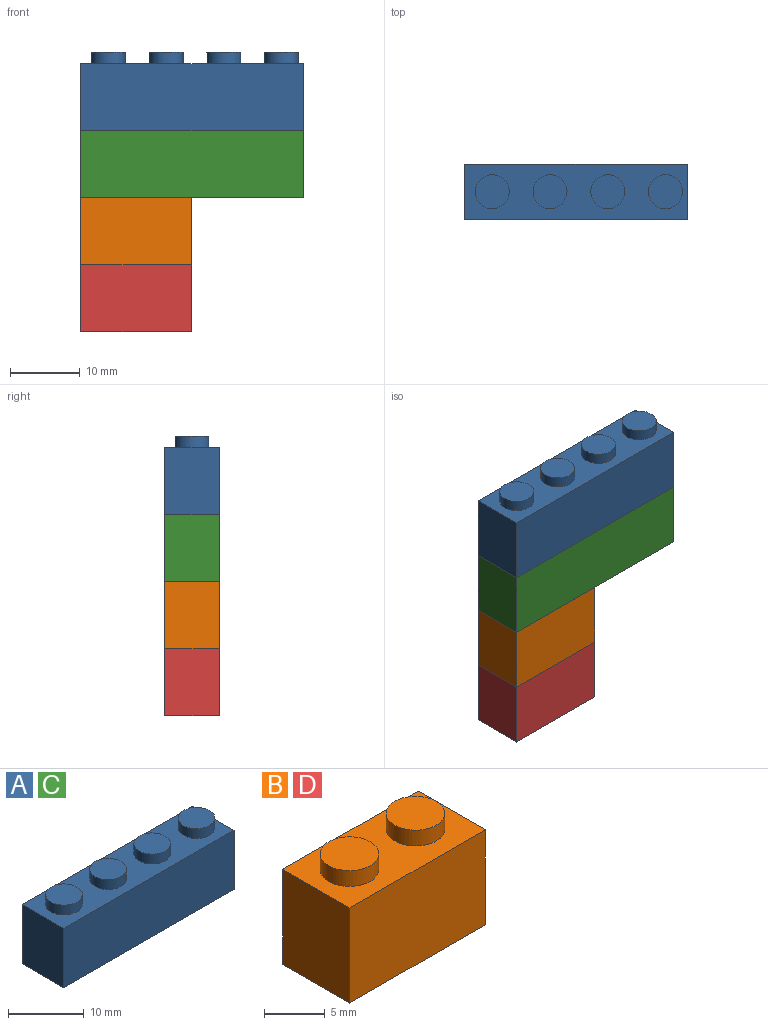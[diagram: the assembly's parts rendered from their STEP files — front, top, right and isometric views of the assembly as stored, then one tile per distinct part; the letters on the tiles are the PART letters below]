
ASSEMBLY  parts=4 mates=4
PART A: 25 faces, bbox 31.8x7.8x11.2 mm
  f0: plane 31.79x7.81mm, normal (0,0,-1), area 110.5mm2, adj f1,f2,f3,f4,f6,f7,f8,f12
  f1: plane 9.58x7.81mm, normal (1,0,0), area 74.8mm2, adj f0,f2,f4,f5
  f2: plane 31.79x9.58mm, normal (0,1,0), area 304.5mm2, adj f0,f1,f3,f5
  f3: plane 9.58x7.81mm, normal (-1,0,0), area 74.8mm2, adj f0,f2,f4,f5
  f4: plane 31.79x9.58mm, normal (0,-1,0), area 304.5mm2, adj f0,f1,f3,f5
  f5: plane 31.79x7.81mm, normal (0,0,1), area 174.1mm2, adj f1,f2,f3,f4,f17,f19,f21,f23
  f6: plane 28.77x8.05mm, normal (0,1,0), area 231.6mm2, adj f0,f7,f12,f13
  f7: plane 8.05x4.79mm, normal (1,0,0), area 38.6mm2, adj f0,f6,f8,f13
  f8: plane 28.77x8.05mm, normal (0,-1,0), area 231.6mm2, adj f0,f7,f12,f13
  f9: cylinder r=1.5mm len=8.05mm, axis (0,0,-1), area 75.6mm2, adj f13,f16
  f10: cylinder r=1.5mm len=8.05mm, axis (0,0,-1), area 75.6mm2, adj f13,f15
  f11: cylinder r=1.5mm len=8.05mm, axis (0,0,-1), area 75.6mm2, adj f13,f14
  f12: plane 8.05x4.79mm, normal (-1,0,0), area 38.6mm2, adj f0,f6,f8,f13
  f13: plane 28.77x4.79mm, normal (0,0,-1), area 116.7mm2, adj f6,f7,f8,f9,f10,f11,f12
  f14: plane 2.99x2.99mm, normal (0,0,-1), area 7mm2, adj f11
  f15: plane 2.99x2.99mm, normal (0,0,-1), area 7mm2, adj f10
  f16: plane 2.99x2.99mm, normal (0,0,-1), area 7mm2, adj f9
  f17: cylinder r=2.43mm len=4.86mm, axis (0,0,-1), area 24.3mm2, adj f5,f18
  f18: plane 4.86x4.86mm, normal (0,0,1), area 18.6mm2, adj f17
  f19: cylinder r=2.43mm len=4.86mm, axis (0,0,-1), area 24.3mm2, adj f5,f20
  f20: plane 4.86x4.86mm, normal (0,0,1), area 18.6mm2, adj f19
  f21: cylinder r=2.43mm len=4.86mm, axis (0,0,-1), area 24.3mm2, adj f5,f22
  f22: plane 4.86x4.86mm, normal (0,0,1), area 18.6mm2, adj f21
  f23: cylinder r=2.43mm len=4.86mm, axis (0,0,-1), area 24.3mm2, adj f5,f24
  f24: plane 4.86x4.86mm, normal (0,0,1), area 18.6mm2, adj f23
PART B: 17 faces, bbox 15.8x7.8x11.2 mm
  f0: plane 15.8x7.81mm, normal (0,0,-1), area 60.4mm2, adj f1,f2,f3,f4,f10,f11,f12,f13
  f1: plane 15.8x9.58mm, normal (0,1,0), area 151.4mm2, adj f0,f2,f4,f5
  f2: plane 9.58x7.81mm, normal (-1,0,0), area 74.8mm2, adj f0,f1,f3,f5
  f3: plane 15.8x9.58mm, normal (0,-1,0), area 151.4mm2, adj f0,f2,f4,f5
  f4: plane 9.58x7.81mm, normal (1,0,0), area 74.8mm2, adj f0,f1,f3,f5
  f5: plane 15.8x7.81mm, normal (0,0,1), area 86.8mm2, adj f1,f2,f3,f4,f6,f8
  f6: cylinder r=2.42mm len=4.83mm, axis (0,0,-1), area 24.1mm2, adj f5,f7
  f7: plane 4.83x4.83mm, normal (0,0,1), area 18.3mm2, adj f6
  f8: cylinder r=2.42mm len=4.83mm, axis (0,0,-1), area 24.1mm2, adj f5,f9
  f9: plane 4.83x4.83mm, normal (0,0,1), area 18.3mm2, adj f8
  f10: plane 12.88x8.18mm, normal (0,1,0), area 105.4mm2, adj f0,f11,f13,f14
  f11: plane 8.18x4.89mm, normal (1,0,0), area 40mm2, adj f0,f10,f12,f14
  f12: plane 12.88x8.18mm, normal (0,-1,0), area 105.4mm2, adj f0,f11,f13,f14
  f13: plane 8.18x4.89mm, normal (-1,0,0), area 40mm2, adj f0,f10,f12,f14
  f14: plane 12.88x4.89mm, normal (0,0,-1), area 55.7mm2, adj f10,f11,f12,f13,f16
  f15: plane 3.04x3.04mm, normal (0,0,-1), area 7.3mm2, adj f16
  f16: cylinder r=1.52mm len=8.18mm, axis (0,0,-1), area 78.1mm2, adj f14,f15
PART C: same geometry as A
PART D: same geometry as B
PLACE A t=(-27.99,-46.15,15.39)mm
PLACE B t=(-31.15,-32.11,-13.35)mm
PLACE C t=(-27.99,-46.15,5.81)mm
PLACE D t=(-31.15,-32.11,-22.93)mm
MATE fastened C.f1 <-> C.f1  axis (1,0,0) through (12,-7.58,-3.77)mm
MATE fastened B.f5 <-> C.f0  axis (0,0,1) through (-19.79,-15.39,-3.77)mm
MATE fastened C.f4 <-> A.f4  axis (0,-1,0) through (-19.79,-15.39,5.81)mm
MATE fastened D.f3 <-> B.f3  axis (0,-1,0) through (-19.79,-15.39,-13.35)mm
